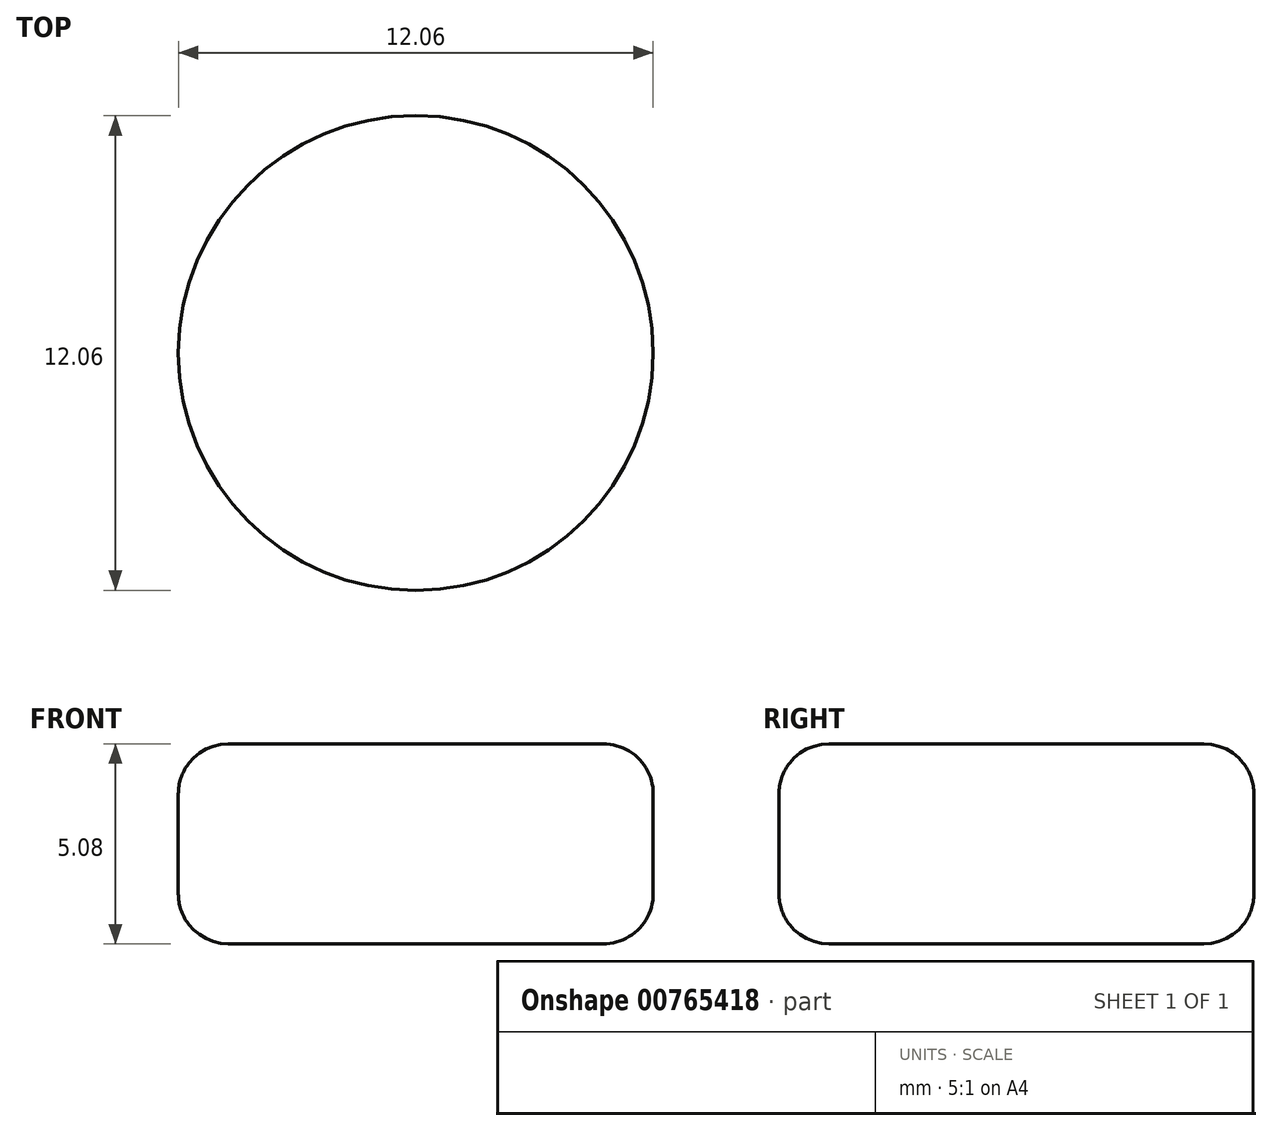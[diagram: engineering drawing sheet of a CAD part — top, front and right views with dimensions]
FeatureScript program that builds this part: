
annotation { "Feature Type Name" : "Feature", "Feature Type Description" : "" }
export const myFeature = defineFeature(function(context is Context, id is Id, definition is map)
    precondition{}
    {
        {
            var Q0;
            Q0=qCreatedBy(makeId("Top.planeOp"),FACE);
            var sketch = newSketch(context, id + "F0", { "sketchPlane" : qUnion([Q0])});
            skPoint(sketch, "E0", {"position": v(0, 0) * mm});
            skCircle(sketch, "E1", {"center": v(0, 0) * mm, "radius": 6.03 * mm});
            skSolve(sketch);
        }
        {
            var Q0;
            Q0=makeQuery(id+"F0.imprint","IMPRINT",FACE,{"disambiguationData":[TD([[makeQuery(id+"F0.imprint","IMPRINT",EDGE,{"derivedFrom":sQuery(id+"F0.wireOp",EDGE,"E1")}),1.0]])]});
            extrude(context, id + "F1", {"entities" : qUnion([Q0]), "depth" : 5.08 * mm, "offsetDistance" : 25.4 * mm});
        }
        {
            var Q0;
            Q0=makeQuery(id+"F1.opExtrude","CAP_EDGE",EDGE,{"disambiguationData":[OSD([sQuery(id+"F0.wireOp",EDGE,"E1")])],"isStart":false});
            var Q1;
            Q1=makeQuery(id+"F1.opExtrude","CAP_EDGE",EDGE,{"disambiguationData":[OSD([sQuery(id+"F0.wireOp",EDGE,"E1")])],"isStart":true});
            fillet(context, id + "F2", {"entities" : qUnion([Q0, Q1]), "radius" : 1.27 * mm, "tangentPropagation" : true, "allowEdgeOverflow" : false});
        }
    });
